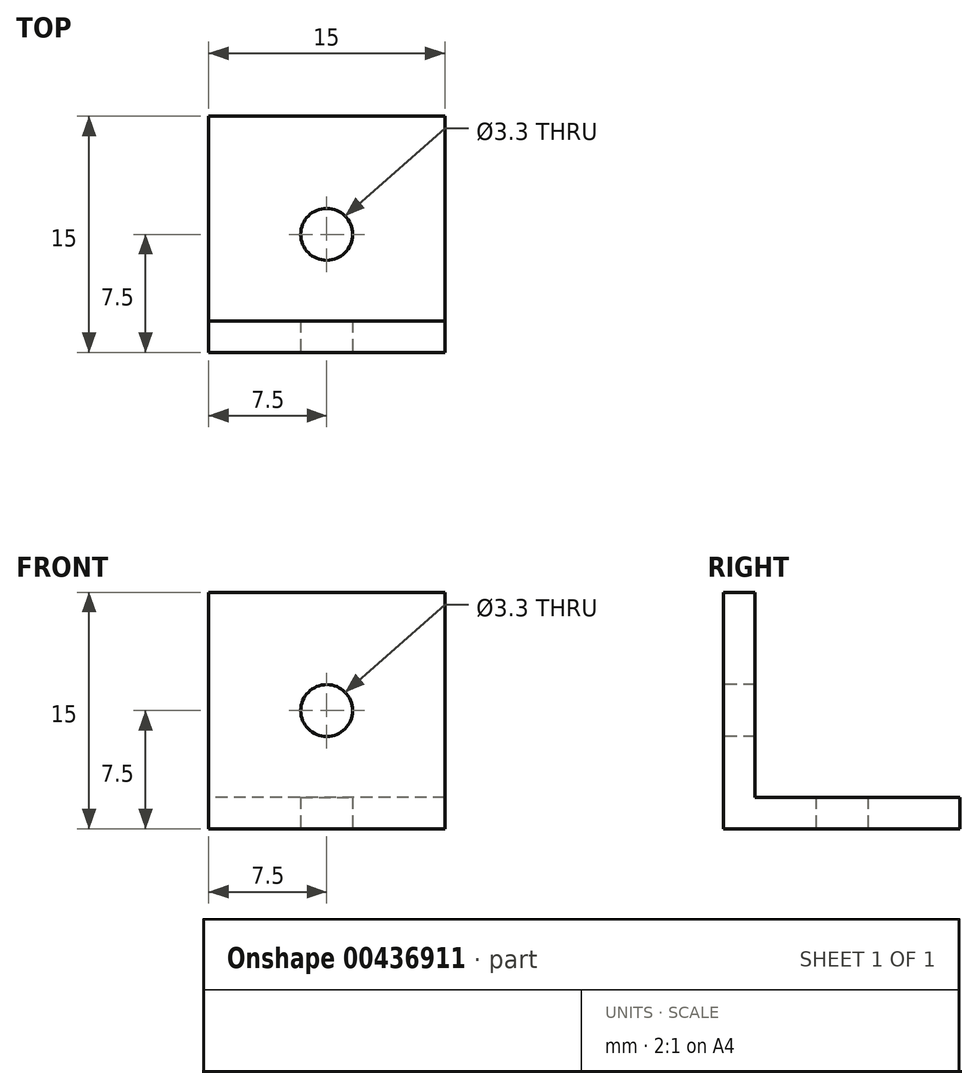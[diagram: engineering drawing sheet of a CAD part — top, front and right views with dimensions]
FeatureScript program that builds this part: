
annotation { "Feature Type Name" : "Feature", "Feature Type Description" : "" }
export const myFeature = defineFeature(function(context is Context, id is Id, definition is map)
    precondition{}
    {
        {
            var Q0;
            Q0=qCreatedBy(makeId("Right.planeOp"),FACE);
            var sketch = newSketch(context, id + "F0", { "sketchPlane" : qUnion([Q0])});
            skLineSegment(sketch, "E0", {"start": v(0, 0) * mm, "end": v(15, 0) * mm});
            skLineSegment(sketch, "E1", {"start": v(15, 0) * mm, "end": v(15, 2) * mm});
            skLineSegment(sketch, "E2", {"start": v(15, 2) * mm, "end": v(2, 2) * mm});
            skLineSegment(sketch, "E3", {"start": v(2, 2) * mm, "end": v(2, 15) * mm});
            skLineSegment(sketch, "E4", {"start": v(2, 15) * mm, "end": v(0, 15) * mm});
            skLineSegment(sketch, "E5", {"start": v(0, 15) * mm, "end": v(0, 0) * mm});
            skSolve(sketch);
        }
        {
            var Q0;
            Q0 = qSketchRegion(id + "F0", true);
            extrude(context, id + "F1", {"entities" : qUnion([Q0]), "depth" : 15 * mm});
        }
        {
            var Q0;
            Q0=makeQuery(id+"F1.opExtrude","SWEPT_FACE",FACE,{"disambiguationData":[OSD([sQuery(id+"F0.wireOp",EDGE,"E0")])]});
            var sketch = newSketch(context, id + "F2", { "sketchPlane" : qUnion([Q0])});
            skPoint(sketch, "E6", {"position": v(7.5, -7.5) * mm});
            skSolve(sketch);
        }
        {
            var Q0;
            Q0=sQuery(id+"F2.wireOp",VERTEX,"E6");
            var Q1;
            Q1=makeQuery(id+"F1.opExtrude","SWEPT_BODY",BODY,{"disambiguationData":[OSD([sQuery(id+"F0.wireOp",EDGE,"E0"),sQuery(id+"F0.wireOp",EDGE,"E1"),sQuery(id+"F0.wireOp",EDGE,"E2"),sQuery(id+"F0.wireOp",EDGE,"E3"),sQuery(id+"F0.wireOp",EDGE,"E4"),sQuery(id+"F0.wireOp",EDGE,"E5")])]});
            hole(context, id + "F3", {"style" : HoleStyle.SIMPLE, "endStyle" : HoleEndStyle.THROUGH, "standardTappedOrClearance" : lookupTablePath({ "standard" : "ISO", "engagement" : "75%", "pitch" : "0.7 mm", "size" : "M4", "type" : "Tapped" }), "standardBlindInLast" : lookupTablePath({ "standard" : "ISO", "engagement" : "75%", "pitch" : "0.7 mm", "size" : "M4", "type" : "Tapped" }), "holeDiameter" : 3.3 * mm, "showTappedDepth" : true, "isTappedThrough" : true, "tappedDepth" : 12 * mm, "tapClearance" : 3, "locations" : qUnion([Q0]), "scope" : qUnion([Q1]), "majorDiameter" : 4 * mm});
        }
        {
            var Q0;
            Q0=makeQuery(id+"F1.opExtrude","SWEPT_FACE",FACE,{"disambiguationData":[OSD([sQuery(id+"F0.wireOp",EDGE,"E5")])]});
            var sketch = newSketch(context, id + "F4", { "sketchPlane" : qUnion([Q0])});
            skPoint(sketch, "E7", {"position": v(7.5, 7.5) * mm});
            skSolve(sketch);
        }
        {
            var Q0;
            Q0=sQuery(id+"F4.wireOp",VERTEX,"E7");
            var Q1;
            Q1=makeQuery(id+"F1.opExtrude","SWEPT_BODY",BODY,{"disambiguationData":[OSD([sQuery(id+"F0.wireOp",EDGE,"E0"),sQuery(id+"F0.wireOp",EDGE,"E1"),sQuery(id+"F0.wireOp",EDGE,"E2"),sQuery(id+"F0.wireOp",EDGE,"E3"),sQuery(id+"F0.wireOp",EDGE,"E4"),sQuery(id+"F0.wireOp",EDGE,"E5")])]});
            hole(context, id + "F5", {"style" : HoleStyle.SIMPLE, "endStyle" : HoleEndStyle.THROUGH, "standardTappedOrClearance" : lookupTablePath({ "standard" : "ISO", "engagement" : "75%", "pitch" : "0.7 mm", "size" : "M4", "type" : "Tapped" }), "standardBlindInLast" : lookupTablePath({ "standard" : "ISO", "engagement" : "75%", "pitch" : "0.7 mm", "size" : "M4", "type" : "Tapped" }), "holeDiameter" : 3.3 * mm, "showTappedDepth" : true, "isTappedThrough" : true, "tappedDepth" : 12 * mm, "tapClearance" : 3, "locations" : qUnion([Q0]), "scope" : qUnion([Q1]), "majorDiameter" : 4 * mm});
        }
    });
